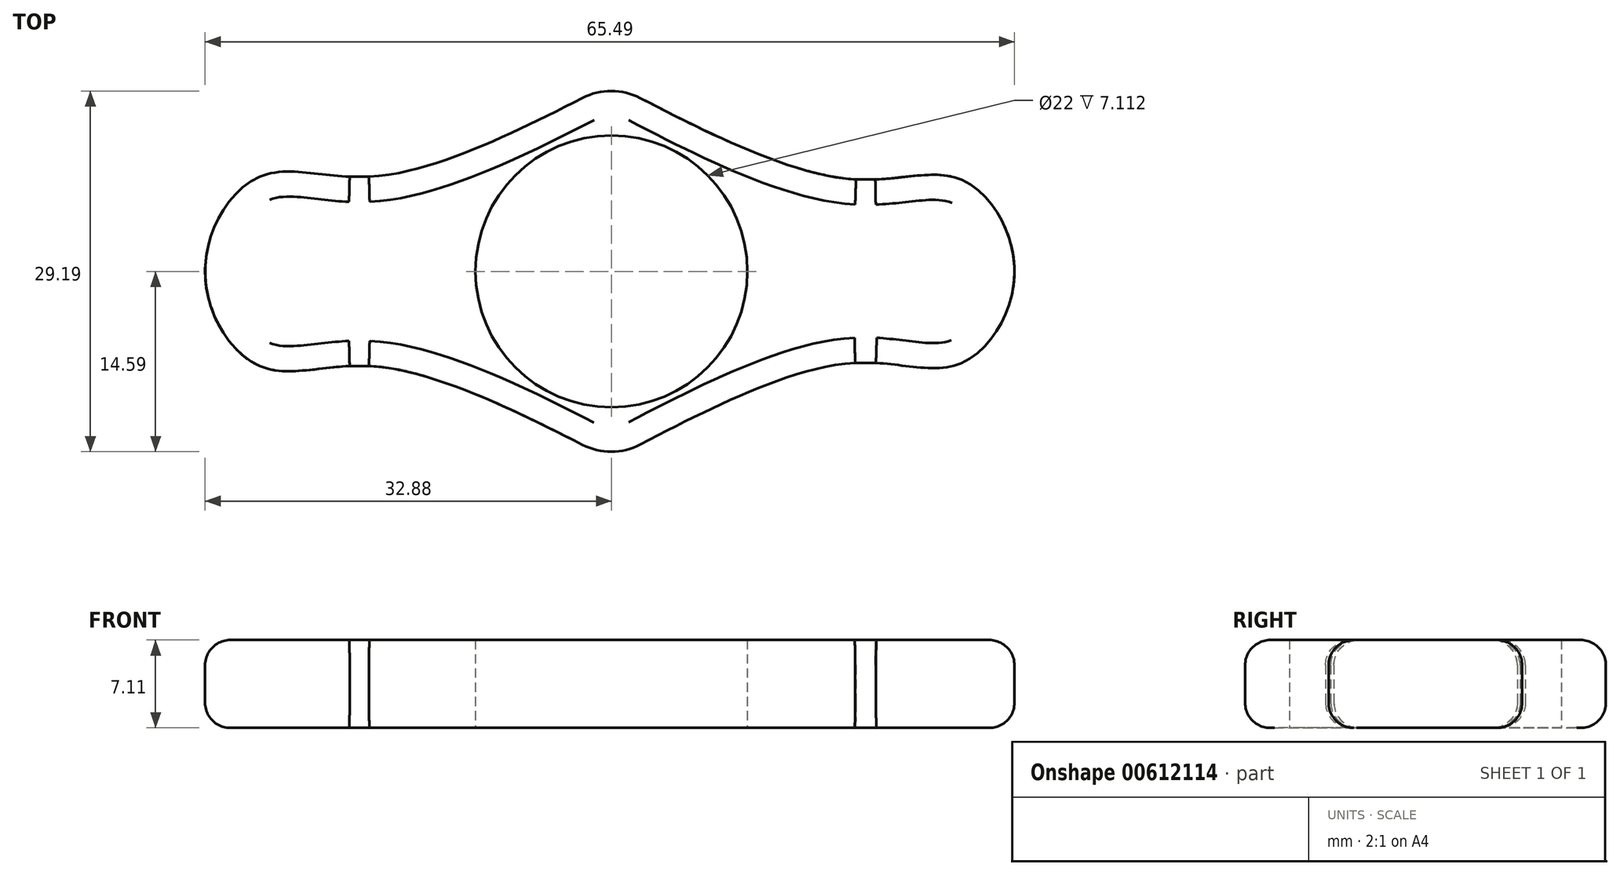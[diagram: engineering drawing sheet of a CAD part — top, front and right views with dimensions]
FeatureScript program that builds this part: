
annotation { "Feature Type Name" : "Feature", "Feature Type Description" : "" }
export const myFeature = defineFeature(function(context is Context, id is Id, definition is map)
    precondition{}
    {
        {
            var Q0;
            Q0=qCreatedBy(makeId("Top.planeOp"),FACE);
            var sketch = newSketch(context, id + "F0", { "sketchPlane" : qUnion([Q0])});
            skLineSegment(sketch, "E0.bottom", {"start": v(35.56, -15.24) * mm, "end": v(-35.56, -15.24) * mm});
            skLineSegment(sketch, "E0.left", {"start": v(35.56, -15.24) * mm, "end": v(35.56, 15.24) * mm});
            skPoint(sketch, "E0.middle", {"position": v(0, 0) * mm});
            skCircle(sketch, "E1", {"center": v(0, 0) * mm, "radius": 11 * mm});
            skLineSegment(sketch, "E2", {"start": v(11, 0) * mm, "end": v(24.04, 0) * mm});
            skArc(sketch, "E3.cCircle", {"start": v(16.62, 0) * mm, "mid": v(18.78, -5.24) * mm, "end": v(24, -7.42) * mm, "construction": true});
            skLineSegment(sketch, "E3.1", {"start": v(28.3, -7.44) * mm, "end": v(19.72, -7.4) * mm});
            skLineSegment(sketch, "E3.2", {"start": v(19.72, -7.4) * mm, "end": v(15.47, 0.04) * mm});
            skLineSegment(sketch, "E3.4", {"start": v(19.79, 7.44) * mm, "end": v(28.36, 7.4) * mm});
            skPoint(sketch, "E3.0.midPoint", {"position": v(30.45, -3.74) * mm});
            skLineSegment(sketch, "E4.3", {"start": v(-28.46, 7.66) * mm, "end": v(-19.62, 7.66) * mm});
            skPoint(sketch, "E4.0.midPoint", {"position": v(-24.04, -7.66) * mm});
            skFitSpline(sketch, "E5", {"points": [v(0, 15.24) * mm, v(-19.62, 7.66) * mm, v(-28.46, 7.66) * mm, v(-32.88, 0) * mm, v(-28.46, -7.66) * mm, v(-19.62, -7.66) * mm, v(0, -15.24) * mm], "startDerivative": vector(-97.51, -50.27) * mm, "endDerivative": vector(97.51, -50.27) * mm});
            skFitSpline(sketch, "E6", {"points": [v(0, 15.24) * mm, v(19.79, 7.44) * mm, v(28.36, 7.4) * mm, v(32.6, -0.04) * mm, v(28.3, -7.44) * mm, v(19.72, -7.4) * mm, v(0, -15.24) * mm], "startDerivative": vector(97.6, -50.94) * mm, "endDerivative": vector(-97.37, -51.4) * mm});
            skPoint(sketch, "E7.orphan", {"position": v(-11, 0) * mm});
            skPoint(sketch, "E4.cCircle.center.orphan", {"position": v(-24.04, 0) * mm});
            skLineSegment(sketch, "E8", {"start": v(-19.62, -7.66) * mm, "end": v(-28.46, -7.66) * mm});
            skPoint(sketch, "E0.right.end.orphan", {"position": v(-35.56, 15.24) * mm});
            skSolve(sketch);
        }
        {
            var Q0;
            Q0 = qSketchRegion(id + "F0", true);
            extrude(context, id + "F1", {"entities" : qUnion([Q0]), "depth" : 7.11 * mm, "offsetDistance" : 25.4 * mm});
        }
        {
            var Q0;
            Q0=makeQuery(id+"F1.opExtrude","SWEPT_EDGE",EDGE,{"disambiguationData":[OSD([sQuery(id+"F0.wireOp",EDGE,"E5"),sQuery(id+"F0.wireOp",EDGE,"E6")])]});
            var Q1;
            Q1=makeQuery(id+"F1.opExtrude","SWEPT_EDGE",EDGE,{"disambiguationData":[OSD([sQuery(id+"F0.wireOp",EDGE,"E6"),sQuery(id+"F0.wireOp",EDGE,"E5")])]});
            fillet(context, id + "F2", {"entities" : qUnion([Q0, Q1]), "radius" : 5.08 * mm, "tangentPropagation" : true, "allowEdgeOverflow" : false});
        }
        {
            var Q0;
            {var subQ0=sQuery(id+"F0.wireOp",EDGE,"E6");var subQ1=sQuery(id+"F0.wireOp",EDGE,"E3.1");var subQ2=makeQuery(id+"F0.imprint","INTERSECT",VERTEX,{"disambiguationData":[OD(0.0)],"derivedFrom":[subQ1,subQ0]});var subQ3=sQuery(id+"F0.wireOp",EDGE,"E3.4");var subQ4=makeQuery(id+"F0.imprint","INTERSECT",VERTEX,{"disambiguationData":[OD(1.0)],"derivedFrom":[subQ3,subQ0]});Q0=makeQuery(id+"F1.opExtrude","CAP_EDGE",EDGE,{"disambiguationData":[OSD([subQ0]),TDD([makeQuery(id+"F0.imprint","IMPRINT",EDGE,{"disambiguationData":[TD([[subQ4,1.0]])],"derivedFrom":subQ0}),makeQuery(id+"F0.imprint","IMPRINT",EDGE,{"disambiguationData":[TD([[subQ2,1.0]])],"derivedFrom":subQ0}),makeQuery(id+"F0.imprint","IMPRINT",EDGE,{"disambiguationData":[TD([[subQ2,-1.0]])],"derivedFrom":subQ0})])],"isStart":false});}
            var Q1;
            {var subQ0=sQuery(id+"F0.wireOp",EDGE,"E6");Q1=makeQuery(id+"F1.opExtrude","CAP_EDGE",EDGE,{"disambiguationData":[OSD([subQ0]),TDD([makeQuery(id+"F0.imprint","IMPRINT",EDGE,{"disambiguationData":[TD([[makeQuery(id+"F0.imprint","INTERSECT",VERTEX,{"disambiguationData":[OD(1.0)],"derivedFrom":[sQuery(id+"F0.wireOp",EDGE,"E3.1"),subQ0]}),-1.0]])],"derivedFrom":subQ0})])],"isStart":false});}
            var Q2;
            Q2=makeQuery(id+"F1.opExtrude","CAP_EDGE",EDGE,{"disambiguationData":[OSD([sQuery(id+"F0.wireOp",EDGE,"E3.1")])],"isStart":false});
            var Q3;
            Q3=makeQuery(id+"F1.opExtrude","CAP_EDGE",EDGE,{"disambiguationData":[OSD([sQuery(id+"F0.wireOp",EDGE,"E3.4")])],"isStart":false});
            var Q4;
            {var subQ0=sQuery(id+"F0.wireOp",EDGE,"E6");Q4=makeQuery(id+"F1.opExtrude","CAP_EDGE",EDGE,{"disambiguationData":[OSD([subQ0]),TDD([makeQuery(id+"F0.imprint","IMPRINT",EDGE,{"disambiguationData":[TD([[makeQuery(id+"F0.imprint","INTERSECT",VERTEX,{"disambiguationData":[OD(0.0)],"derivedFrom":[sQuery(id+"F0.wireOp",EDGE,"E3.4"),subQ0]}),1.0]])],"derivedFrom":subQ0})])],"isStart":false});}
            var Q5;
            {var subQ0=sQuery(id+"F0.wireOp",EDGE,"E6");var subQ1=sQuery(id+"F0.wireOp",EDGE,"E5");Q5=makeQuery(id+"F2.opFillet","BLEND_EDGE",EDGE,{"blendedFrom":[makeQuery(id+"F1.opExtrude","SWEPT_EDGE",EDGE,{"disambiguationData":[OSD([subQ1,subQ0])]}),makeQuery(id+"F1.opExtrude","CAP_FACE",FACE,{"disambiguationData":[OSD([sQuery(id+"F0.wireOp",EDGE,"E1"),sQuery(id+"F0.wireOp",EDGE,"E3.1"),sQuery(id+"F0.wireOp",EDGE,"E3.4"),sQuery(id+"F0.wireOp",EDGE,"E4.3"),subQ1,subQ0,sQuery(id+"F0.wireOp",EDGE,"E5"),sQuery(id+"F0.wireOp",EDGE,"E8")])],"isStart":false})],"blendedInto":[makeQuery(id+"F1.opExtrude","CAP_FACE",FACE,{"disambiguationData":[OSD([sQuery(id+"F0.wireOp",EDGE,"E1"),sQuery(id+"F0.wireOp",EDGE,"E3.1"),sQuery(id+"F0.wireOp",EDGE,"E3.4"),sQuery(id+"F0.wireOp",EDGE,"E4.3"),subQ1,subQ0,sQuery(id+"F0.wireOp",EDGE,"E5"),sQuery(id+"F0.wireOp",EDGE,"E8")])],"isStart":false})]});}
            var Q6;
            {var subQ0=sQuery(id+"F0.wireOp",EDGE,"E5");Q6=makeQuery(id+"F1.opExtrude","CAP_EDGE",EDGE,{"disambiguationData":[OSD([subQ0]),TDD([makeQuery(id+"F0.imprint","IMPRINT",EDGE,{"disambiguationData":[TD([[makeQuery(id+"F0.imprint","INTERSECT",VERTEX,{"disambiguationData":[OD(1.0)],"derivedFrom":[sQuery(id+"F0.wireOp",EDGE,"E4.3"),subQ0]}),1.0]])],"derivedFrom":subQ0})])],"isStart":false});}
            var Q7;
            {var subQ0=sQuery(id+"F0.wireOp",EDGE,"E5");var subQ1=sQuery(id+"F0.wireOp",EDGE,"E4.3");var subQ2=makeQuery(id+"F0.imprint","INTERSECT",VERTEX,{"disambiguationData":[OD(0.0)],"derivedFrom":[subQ1,subQ0]});Q7=makeQuery(id+"F1.opExtrude","CAP_EDGE",EDGE,{"disambiguationData":[OSD([subQ0]),TDD([makeQuery(id+"F0.imprint","IMPRINT",EDGE,{"disambiguationData":[TD([[subQ2,1.0]])],"derivedFrom":subQ0}),makeQuery(id+"F0.imprint","IMPRINT",EDGE,{"disambiguationData":[TD([[subQ2,-1.0]])],"derivedFrom":subQ0})])],"isStart":false});}
            var Q8;
            Q8=makeQuery(id+"F1.opExtrude","CAP_EDGE",EDGE,{"disambiguationData":[OSD([sQuery(id+"F0.wireOp",EDGE,"E4.3")])],"isStart":false});
            var Q9;
            Q9=makeQuery(id+"F1.opExtrude","CAP_EDGE",EDGE,{"disambiguationData":[OSD([sQuery(id+"F0.wireOp",EDGE,"E8")])],"isStart":false});
            var Q10;
            Q10=makeQuery(id+"F1.opExtrude","CAP_EDGE",EDGE,{"disambiguationData":[OSD([sQuery(id+"F0.wireOp",EDGE,"E5")])],"isStart":false});
            var Q11;
            {var subQ0=sQuery(id+"F0.wireOp",EDGE,"E5");var subQ1=sQuery(id+"F0.wireOp",EDGE,"E6");Q11=makeQuery(id+"F2.opFillet","BLEND_EDGE",EDGE,{"blendedFrom":[makeQuery(id+"F1.opExtrude","SWEPT_EDGE",EDGE,{"disambiguationData":[OSD([subQ1,subQ0])]}),makeQuery(id+"F1.opExtrude","CAP_FACE",FACE,{"disambiguationData":[OSD([sQuery(id+"F0.wireOp",EDGE,"E1"),sQuery(id+"F0.wireOp",EDGE,"E3.1"),sQuery(id+"F0.wireOp",EDGE,"E3.4"),sQuery(id+"F0.wireOp",EDGE,"E4.3"),sQuery(id+"F0.wireOp",EDGE,"E5"),subQ1,subQ0,sQuery(id+"F0.wireOp",EDGE,"E8")])],"isStart":false})],"blendedInto":[makeQuery(id+"F1.opExtrude","CAP_FACE",FACE,{"disambiguationData":[OSD([sQuery(id+"F0.wireOp",EDGE,"E1"),sQuery(id+"F0.wireOp",EDGE,"E3.1"),sQuery(id+"F0.wireOp",EDGE,"E3.4"),sQuery(id+"F0.wireOp",EDGE,"E4.3"),sQuery(id+"F0.wireOp",EDGE,"E5"),subQ1,subQ0,sQuery(id+"F0.wireOp",EDGE,"E8")])],"isStart":false})]});}
            var Q12;
            {var subQ0=sQuery(id+"F0.wireOp",EDGE,"E6");var subQ1=sQuery(id+"F0.wireOp",EDGE,"E3.1");var subQ2=makeQuery(id+"F0.imprint","INTERSECT",VERTEX,{"disambiguationData":[OD(0.0)],"derivedFrom":[subQ1,subQ0]});var subQ3=sQuery(id+"F0.wireOp",EDGE,"E3.4");var subQ4=makeQuery(id+"F0.imprint","INTERSECT",VERTEX,{"disambiguationData":[OD(1.0)],"derivedFrom":[subQ3,subQ0]});Q12=makeQuery(id+"F1.opExtrude","CAP_EDGE",EDGE,{"disambiguationData":[OSD([subQ0]),TDD([makeQuery(id+"F0.imprint","IMPRINT",EDGE,{"disambiguationData":[TD([[subQ4,1.0]])],"derivedFrom":subQ0}),makeQuery(id+"F0.imprint","IMPRINT",EDGE,{"disambiguationData":[TD([[subQ2,1.0]])],"derivedFrom":subQ0}),makeQuery(id+"F0.imprint","IMPRINT",EDGE,{"disambiguationData":[TD([[subQ2,-1.0]])],"derivedFrom":subQ0})])],"isStart":true});}
            var Q13;
            {var subQ0=sQuery(id+"F0.wireOp",EDGE,"E6");Q13=makeQuery(id+"F1.opExtrude","CAP_EDGE",EDGE,{"disambiguationData":[OSD([subQ0]),TDD([makeQuery(id+"F0.imprint","IMPRINT",EDGE,{"disambiguationData":[TD([[makeQuery(id+"F0.imprint","INTERSECT",VERTEX,{"disambiguationData":[OD(0.0)],"derivedFrom":[sQuery(id+"F0.wireOp",EDGE,"E3.4"),subQ0]}),1.0]])],"derivedFrom":subQ0})])],"isStart":true});}
            var Q14;
            Q14=makeQuery(id+"F1.opExtrude","CAP_EDGE",EDGE,{"disambiguationData":[OSD([sQuery(id+"F0.wireOp",EDGE,"E3.4")])],"isStart":true});
            var Q15;
            Q15=makeQuery(id+"F1.opExtrude","CAP_EDGE",EDGE,{"disambiguationData":[OSD([sQuery(id+"F0.wireOp",EDGE,"E3.1")])],"isStart":true});
            var Q16;
            {var subQ0=sQuery(id+"F0.wireOp",EDGE,"E6");Q16=makeQuery(id+"F1.opExtrude","CAP_EDGE",EDGE,{"disambiguationData":[OSD([subQ0]),TDD([makeQuery(id+"F0.imprint","IMPRINT",EDGE,{"disambiguationData":[TD([[makeQuery(id+"F0.imprint","INTERSECT",VERTEX,{"disambiguationData":[OD(1.0)],"derivedFrom":[sQuery(id+"F0.wireOp",EDGE,"E3.1"),subQ0]}),-1.0]])],"derivedFrom":subQ0})])],"isStart":true});}
            var Q17;
            {var subQ0=sQuery(id+"F0.wireOp",EDGE,"E5");var subQ1=sQuery(id+"F0.wireOp",EDGE,"E6");Q17=makeQuery(id+"F2.opFillet","BLEND_EDGE",EDGE,{"blendedFrom":[makeQuery(id+"F1.opExtrude","SWEPT_EDGE",EDGE,{"disambiguationData":[OSD([subQ1,subQ0])]}),makeQuery(id+"F1.opExtrude","CAP_FACE",FACE,{"disambiguationData":[OSD([sQuery(id+"F0.wireOp",EDGE,"E1"),sQuery(id+"F0.wireOp",EDGE,"E3.1"),sQuery(id+"F0.wireOp",EDGE,"E3.4"),sQuery(id+"F0.wireOp",EDGE,"E4.3"),sQuery(id+"F0.wireOp",EDGE,"E5"),subQ1,subQ0,sQuery(id+"F0.wireOp",EDGE,"E8")])],"isStart":true})],"blendedInto":[makeQuery(id+"F1.opExtrude","CAP_FACE",FACE,{"disambiguationData":[OSD([sQuery(id+"F0.wireOp",EDGE,"E1"),sQuery(id+"F0.wireOp",EDGE,"E3.1"),sQuery(id+"F0.wireOp",EDGE,"E3.4"),sQuery(id+"F0.wireOp",EDGE,"E4.3"),sQuery(id+"F0.wireOp",EDGE,"E5"),subQ1,subQ0,sQuery(id+"F0.wireOp",EDGE,"E8")])],"isStart":true})]});}
            var Q18;
            Q18=makeQuery(id+"F1.opExtrude","CAP_EDGE",EDGE,{"disambiguationData":[OSD([sQuery(id+"F0.wireOp",EDGE,"E5")])],"isStart":true});
            var Q19;
            Q19=makeQuery(id+"F1.opExtrude","CAP_EDGE",EDGE,{"disambiguationData":[OSD([sQuery(id+"F0.wireOp",EDGE,"E8")])],"isStart":true});
            var Q20;
            {var subQ0=sQuery(id+"F0.wireOp",EDGE,"E5");var subQ1=sQuery(id+"F0.wireOp",EDGE,"E4.3");var subQ2=makeQuery(id+"F0.imprint","INTERSECT",VERTEX,{"disambiguationData":[OD(0.0)],"derivedFrom":[subQ1,subQ0]});Q20=makeQuery(id+"F1.opExtrude","CAP_EDGE",EDGE,{"disambiguationData":[OSD([subQ0]),TDD([makeQuery(id+"F0.imprint","IMPRINT",EDGE,{"disambiguationData":[TD([[subQ2,1.0]])],"derivedFrom":subQ0}),makeQuery(id+"F0.imprint","IMPRINT",EDGE,{"disambiguationData":[TD([[subQ2,-1.0]])],"derivedFrom":subQ0})])],"isStart":true});}
            var Q21;
            Q21=makeQuery(id+"F1.opExtrude","CAP_EDGE",EDGE,{"disambiguationData":[OSD([sQuery(id+"F0.wireOp",EDGE,"E4.3")])],"isStart":true});
            var Q22;
            {var subQ0=sQuery(id+"F0.wireOp",EDGE,"E5");Q22=makeQuery(id+"F1.opExtrude","CAP_EDGE",EDGE,{"disambiguationData":[OSD([subQ0]),TDD([makeQuery(id+"F0.imprint","IMPRINT",EDGE,{"disambiguationData":[TD([[makeQuery(id+"F0.imprint","INTERSECT",VERTEX,{"disambiguationData":[OD(1.0)],"derivedFrom":[sQuery(id+"F0.wireOp",EDGE,"E4.3"),subQ0]}),1.0]])],"derivedFrom":subQ0})])],"isStart":true});}
            var Q23;
            {var subQ0=sQuery(id+"F0.wireOp",EDGE,"E6");var subQ1=sQuery(id+"F0.wireOp",EDGE,"E5");Q23=makeQuery(id+"F2.opFillet","BLEND_EDGE",EDGE,{"blendedFrom":[makeQuery(id+"F1.opExtrude","SWEPT_EDGE",EDGE,{"disambiguationData":[OSD([subQ1,subQ0])]}),makeQuery(id+"F1.opExtrude","CAP_FACE",FACE,{"disambiguationData":[OSD([sQuery(id+"F0.wireOp",EDGE,"E1"),sQuery(id+"F0.wireOp",EDGE,"E3.1"),sQuery(id+"F0.wireOp",EDGE,"E3.4"),sQuery(id+"F0.wireOp",EDGE,"E4.3"),subQ1,subQ0,sQuery(id+"F0.wireOp",EDGE,"E5"),sQuery(id+"F0.wireOp",EDGE,"E8")])],"isStart":true})],"blendedInto":[makeQuery(id+"F1.opExtrude","CAP_FACE",FACE,{"disambiguationData":[OSD([sQuery(id+"F0.wireOp",EDGE,"E1"),sQuery(id+"F0.wireOp",EDGE,"E3.1"),sQuery(id+"F0.wireOp",EDGE,"E3.4"),sQuery(id+"F0.wireOp",EDGE,"E4.3"),subQ1,subQ0,sQuery(id+"F0.wireOp",EDGE,"E5"),sQuery(id+"F0.wireOp",EDGE,"E8")])],"isStart":true})]});}
            fillet(context, id + "F3", {"entities" : qUnion([Q0, Q1, Q2, Q3, Q4, Q5, Q6, Q7, Q8, Q9, Q10, Q11, Q12, Q13, Q14, Q15, Q16, Q17, Q18, Q19, Q20, Q21, Q22, Q23]), "radius" : 2.03 * mm, "tangentPropagation" : true, "allowEdgeOverflow" : false});
        }
    });
